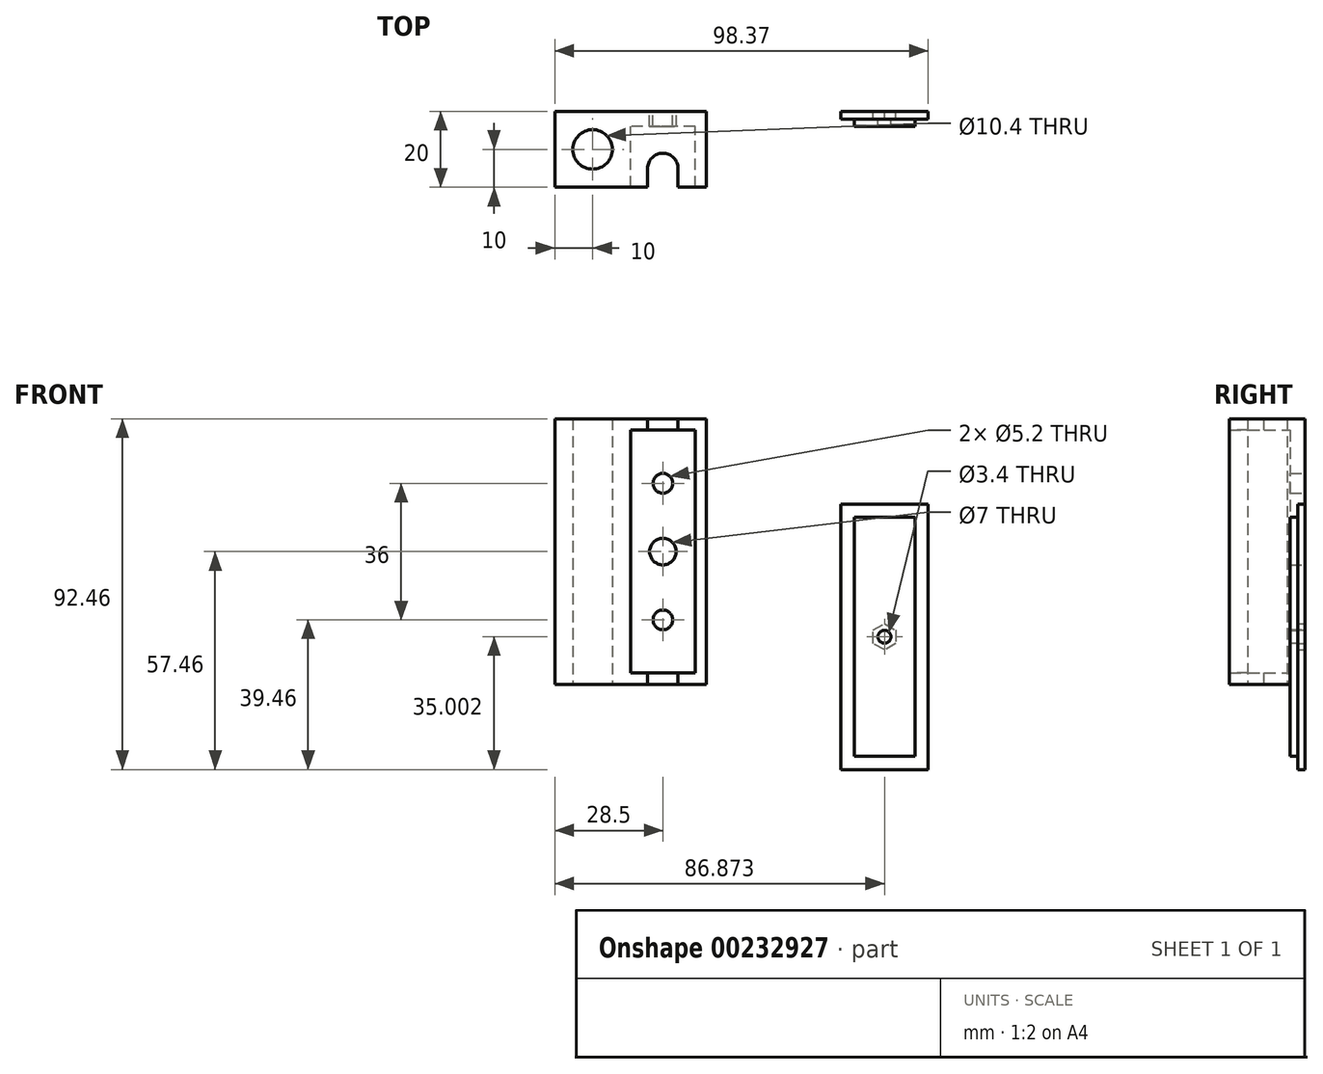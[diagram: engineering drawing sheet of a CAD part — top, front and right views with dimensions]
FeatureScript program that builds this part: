
annotation { "Feature Type Name" : "Feature", "Feature Type Description" : "" }
export const myFeature = defineFeature(function(context is Context, id is Id, definition is map)
    precondition{}
    {
        {
            var Q0;
            Q0=qCreatedBy(makeId("Front.planeOp"),FACE);
            var sketch = newSketch(context, id + "F0", { "sketchPlane" : qUnion([Q0])});
            skLineSegment(sketch, "E0.bottom", {"start": v(0, 0) * mm, "end": v(-40, 0) * mm});
            skLineSegment(sketch, "E0.top", {"start": v(0, 70) * mm, "end": v(-40, 70) * mm});
            skLineSegment(sketch, "E0.left", {"start": v(0, 0) * mm, "end": v(0, 70) * mm});
            skLineSegment(sketch, "E0.right", {"start": v(-40, 0) * mm, "end": v(-40, 70) * mm});
            skLineSegment(sketch, "E1", {"start": v(-20, 70) * mm, "end": v(-20, 0) * mm});
            skLineSegment(sketch, "E2.0", {"start": v(-3, 67) * mm, "end": v(-20, 67) * mm});
            skLineSegment(sketch, "E2.1", {"start": v(-3, 3) * mm, "end": v(-3, 67) * mm});
            skLineSegment(sketch, "E2.2", {"start": v(-3, 3) * mm, "end": v(-20, 3) * mm});
            skLineSegment(sketch, "E3", {"start": v(-3, 35) * mm, "end": v(-20, 35) * mm});
            skCircle(sketch, "E4", {"center": v(-11.5, 35) * mm, "radius": 3.5 * mm});
            skCircle(sketch, "E5", {"center": v(-11.5, 35) * mm, "radius": 1.7 * mm});
            skLineSegment(sketch, "E6", {"start": v(-11.5, 67) * mm, "end": v(-11.5, 53) * mm});
            skLineSegment(sketch, "E7", {"start": v(-11.5, 3) * mm, "end": v(-11.5, 17) * mm});
            skCircle(sketch, "E8", {"center": v(-11.5, 17) * mm, "radius": 2.6 * mm});
            skCircle(sketch, "E9", {"center": v(-11.5, 53) * mm, "radius": 2.6 * mm});
            skSolve(sketch);
        }
        {
            var Q0;
            {var subQ0=sQuery(id+"F0.wireOp",EDGE,"E0.right");Q0=makeQuery(id+"F0.imprint","IMPRINT",FACE,{"disambiguationData":[TD([[makeQuery(id+"F0.imprint","IMPRINT",EDGE,{"derivedFrom":subQ0}),-1.0]])]});}
            var Q1;
            {var subQ4=sQuery(id+"F0.wireOp",EDGE,"E0.left");Q1=makeQuery(id+"F0.imprint","IMPRINT",FACE,{"disambiguationData":[TD([[makeQuery(id+"F0.imprint","IMPRINT",EDGE,{"derivedFrom":subQ4}),1.0]])]});}
            extrude(context, id + "F1", {"entities" : qUnion([Q0, Q1]), "depth" : 20 * mm});
        }
        {
            var Q0;
            {var subQ0=sQuery(id+"F0.wireOp",EDGE,"E2.0");Q0=makeQuery(id+"F0.imprint","IMPRINT",FACE,{"disambiguationData":[TD([[makeQuery(id+"F0.imprint","IMPRINT",EDGE,{"derivedFrom":subQ0}),1.0]])]});}
            var Q1;
            {var subQ5=sQuery(id+"F0.wireOp",EDGE,"E2.2");Q1=makeQuery(id+"F0.imprint","IMPRINT",FACE,{"disambiguationData":[TD([[makeQuery(id+"F0.imprint","IMPRINT",EDGE,{"derivedFrom":subQ5}),-1.0]])]});}
            var Q2;
            {var subQ0=sQuery(id+"F0.wireOp",EDGE,"E4");var subQ1=sQuery(id+"F0.wireOp",EDGE,"E3");var subQ2=makeQuery(id+"F0.imprint","INTERSECT",VERTEX,{"disambiguationData":[OD(0.0)],"derivedFrom":[subQ1,subQ0]});Q2=makeQuery(id+"F0.imprint","IMPRINT",FACE,{"disambiguationData":[TD([[makeQuery(id+"F0.imprint","IMPRINT",EDGE,{"disambiguationData":[TD([[subQ2,-1.0]])],"derivedFrom":subQ1}),-1.0]])]});}
            var Q3;
            {var subQ0=sQuery(id+"F0.wireOp",EDGE,"E4");var subQ1=sQuery(id+"F0.wireOp",EDGE,"E3");var subQ2=makeQuery(id+"F0.imprint","INTERSECT",VERTEX,{"disambiguationData":[OD(0.0)],"derivedFrom":[subQ1,subQ0]});Q3=makeQuery(id+"F0.imprint","IMPRINT",FACE,{"disambiguationData":[TD([[makeQuery(id+"F0.imprint","IMPRINT",EDGE,{"disambiguationData":[TD([[subQ2,-1.0]])],"derivedFrom":subQ1}),1.0]])]});}
            extrude(context, id + "F2", {"entities" : qUnion([Q0, Q1, Q2, Q3]), "operationType" : NewBodyOperationType.ADD, "depth" : 4 * mm});
        }
        {
            var Q0;
            Q0=makeQuery(id+"F1.opExtrude","SWEPT_FACE",FACE,{"disambiguationData":[OSD([sQuery(id+"F0.wireOp",EDGE,"E0.bottom")])]});
            var sketch = newSketch(context, id + "F3", { "sketchPlane" : qUnion([Q0])});
            skLineSegment(sketch, "E10", {"start": v(-11.52, 0) * mm, "end": v(-11.52, 15) * mm});
            skArc(sketch, "E11", {"start": v(-15.52, 15) * mm, "mid": v(-11.52, 11) * mm, "end": v(-7.52, 15) * mm});
            skLineSegment(sketch, "E12", {"start": v(-7.52, 15) * mm, "end": v(-7.52, 20) * mm});
            skLineSegment(sketch, "E13", {"start": v(-15.52, 15) * mm, "end": v(-15.52, 20) * mm});
            skLineSegment(sketch, "E14", {"start": v(-40, 10) * mm, "end": v(-30, 10) * mm});
            skCircle(sketch, "E15", {"center": v(-30, 10) * mm, "radius": 5.2 * mm});
            skSolve(sketch);
        }
        {
            var Q0;
            {var subQ1=sQuery(id+"F3.wireOp",EDGE,"E12");Q0=makeQuery(id+"F3.imprint","IMPRINT",FACE,{"disambiguationData":[TD([[makeQuery(id+"F3.imprint","IMPRINT",EDGE,{"derivedFrom":subQ1}),1.0]])]});}
            extrude(context, id + "F4", {"entities" : qUnion([Q0]), "operationType" : NewBodyOperationType.REMOVE, "oppositeDirection" : true, "depth" : 80 * mm});
        }
        {
            var Q0;
            Q0=qCreatedBy(makeId("Front.planeOp"),FACE);
            var sketch = newSketch(context, id + "F5", { "sketchPlane" : qUnion([Q0])});
            skLineSegment(sketch, "E16.bottom", {"start": v(35.37, -22.46) * mm, "end": v(58.37, -22.46) * mm});
            skLineSegment(sketch, "E16.top", {"start": v(35.37, 47.54) * mm, "end": v(58.37, 47.54) * mm});
            skLineSegment(sketch, "E16.left", {"start": v(35.37, -22.46) * mm, "end": v(35.37, 47.54) * mm});
            skLineSegment(sketch, "E16.right", {"start": v(58.37, -22.46) * mm, "end": v(58.37, 47.54) * mm});
            skPoint(sketch, "E16.middle", {"position": v(46.87, 12.54) * mm});
            skLineSegment(sketch, "E17.bottom", {"start": v(38.87, -18.96) * mm, "end": v(54.87, -18.96) * mm});
            skLineSegment(sketch, "E17.top", {"start": v(38.87, 44.04) * mm, "end": v(54.87, 44.04) * mm});
            skLineSegment(sketch, "E17.left", {"start": v(38.87, -18.96) * mm, "end": v(38.87, 44.04) * mm});
            skLineSegment(sketch, "E17.right", {"start": v(54.87, -18.96) * mm, "end": v(54.87, 44.04) * mm});
            skCircle(sketch, "E18", {"center": v(46.87, 12.54) * mm, "radius": 1.7 * mm});
            skCircle(sketch, "E19.cCircle", {"center": v(46.87, 12.54) * mm, "radius": 3 * mm, "construction": true});
            skPoint(sketch, "E19.cCircle.perimeterSnap0", {"position": v(38.87, 12.54) * mm});
            skLineSegment(sketch, "E19.0", {"start": v(43.87, 10.81) * mm, "end": v(43.87, 14.27) * mm});
            skLineSegment(sketch, "E19.1", {"start": v(43.87, 14.27) * mm, "end": v(46.87, 16) * mm});
            skLineSegment(sketch, "E19.2", {"start": v(46.87, 16) * mm, "end": v(49.87, 14.27) * mm});
            skLineSegment(sketch, "E19.3", {"start": v(49.87, 14.27) * mm, "end": v(49.87, 10.81) * mm});
            skLineSegment(sketch, "E19.4", {"start": v(49.87, 10.81) * mm, "end": v(46.87, 9.08) * mm});
            skLineSegment(sketch, "E19.5", {"start": v(46.87, 9.08) * mm, "end": v(43.87, 10.81) * mm});
            skPoint(sketch, "E19.0.midPoint", {"position": v(43.87, 12.54) * mm});
            skPoint(sketch, "E19.0.midPoint.positionSnap0", {"position": v(38.87, 12.54) * mm});
            skSolve(sketch);
        }
        {
            var Q0;
            Q0=makeQuery(id+"F5.imprint","IMPRINT",FACE,{"disambiguationData":[TD([[makeQuery(id+"F5.imprint","IMPRINT",EDGE,{"derivedFrom":sQuery(id+"F5.wireOp",EDGE,"E16.bottom")}),1.0]])]});
            extrude(context, id + "F6", {"entities" : qUnion([Q0]), "depth" : 2 * mm});
        }
        {
            var Q0;
            Q0=makeQuery(id+"F5.imprint","IMPRINT",FACE,{"disambiguationData":[TD([[makeQuery(id+"F5.imprint","IMPRINT",EDGE,{"derivedFrom":sQuery(id+"F5.wireOp",EDGE,"E17.bottom")}),1.0]])]});
            extrude(context, id + "F7", {"entities" : qUnion([Q0]), "operationType" : NewBodyOperationType.ADD, "depth" : 4 * mm});
        }
        {
            var Q0;
            Q0=makeQuery(id+"F3.imprint","IMPRINT",FACE,{"disambiguationData":[TD([[makeQuery(id+"F3.imprint","IMPRINT",EDGE,{"derivedFrom":sQuery(id+"F3.wireOp",EDGE,"E15")}),1.0]])]});
            extrude(context, id + "F8", {"entities" : qUnion([Q0]), "operationType" : NewBodyOperationType.REMOVE, "oppositeDirection" : true, "depth" : 80 * mm});
        }
        {
            var Q0;
            Q0=makeQuery(id+"F5.imprint","IMPRINT",FACE,{"disambiguationData":[TD([[makeQuery(id+"F5.imprint","IMPRINT",EDGE,{"derivedFrom":sQuery(id+"F5.wireOp",EDGE,"E18")}),-1.0]])]});
            extrude(context, id + "F9", {"entities" : qUnion([Q0]), "operationType" : NewBodyOperationType.ADD, "depth" : 4 * mm});
        }
        {
            var Q0;
            Q0=makeQuery(id+"F5.imprint","IMPRINT",FACE,{"disambiguationData":[TD([[makeQuery(id+"F5.imprint","IMPRINT",EDGE,{"derivedFrom":sQuery(id+"F5.wireOp",EDGE,"E18")}),-1.0]])]});
            extrude(context, id + "F10", {"entities" : qUnion([Q0]), "operationType" : NewBodyOperationType.REMOVE, "depth" : 2 * mm});
        }
    });
